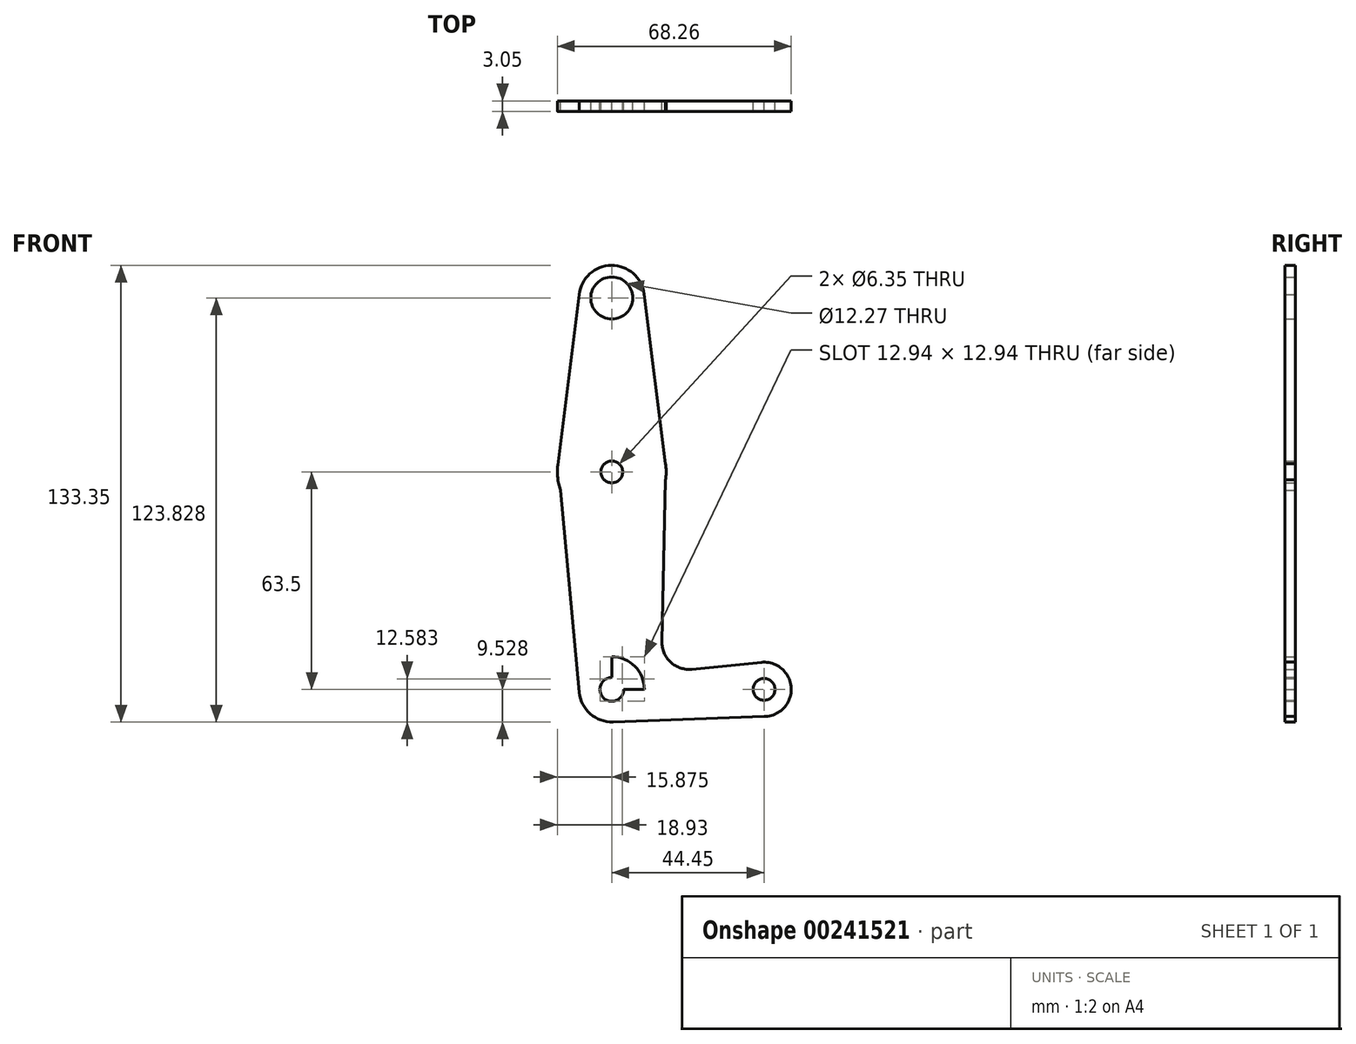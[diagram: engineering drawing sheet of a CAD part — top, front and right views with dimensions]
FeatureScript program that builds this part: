
annotation { "Feature Type Name" : "Feature", "Feature Type Description" : "" }
export const myFeature = defineFeature(function(context is Context, id is Id, definition is map)
    precondition{}
    {
        {
            var Q0;
            Q0=qCreatedBy(makeId("Front.planeOp"),FACE);
            var sketch = newSketch(context, id + "F0", { "sketchPlane" : qUnion([Q0])});
            skLineSegment(sketch, "E0", {"start": v(-63.28, 63.3) * mm, "end": v(-63.28, -51) * mm});
            skLineSegment(sketch, "E1", {"start": v(-63.28, -51) * mm, "end": v(-18.83, -51) * mm});
            skCircle(sketch, "E2", {"center": v(-63.28, 63.3) * mm, "radius": 9.53 * mm});
            skCircle(sketch, "E3", {"center": v(-63.28, 12.5) * mm, "radius": 15.88 * mm});
            skCircle(sketch, "E4", {"center": v(-63.28, -51) * mm, "radius": 9.53 * mm});
            skCircle(sketch, "E5", {"center": v(-18.83, -51) * mm, "radius": 7.94 * mm});
            skLineSegment(sketch, "E6", {"start": v(-41.05, -51) * mm, "end": v(-56.61, -51) * mm});
            skLineSegment(sketch, "E7", {"start": v(-63.28, 12.5) * mm, "end": v(-63.28, -51) * mm});
            skLineSegment(sketch, "E8", {"start": v(-72.75, 64.3) * mm, "end": v(-79.03, 14.48) * mm});
            skLineSegment(sketch, "E9", {"start": v(-78.24, 7.21) * mm, "end": v(-72.76, -51.88) * mm});
            skLineSegment(sketch, "E10", {"start": v(-47.48, 14.1) * mm, "end": v(-53.82, 64.49) * mm});
            skCircle(sketch, "E11", {"center": v(-63.28, 63.3) * mm, "radius": 6.13 * mm});
            skCircle(sketch, "E12", {"center": v(-63.28, 12.5) * mm, "radius": 3.18 * mm});
            skCircle(sketch, "E13", {"center": v(-63.28, -51) * mm, "radius": 3.48 * mm});
            skCircle(sketch, "E14", {"center": v(-18.83, -51) * mm, "radius": 3.18 * mm});
            skLineSegment(sketch, "E15", {"start": v(-18.83, -58.94) * mm, "end": v(-62.93, -60.52) * mm});
            skLineSegment(sketch, "E16", {"start": v(-19.62, -43.1) * mm, "end": v(-39.89, -45.14) * mm});
            skPoint(sketch, "E16.endSnap0", {"position": v(-48.83, -51) * mm});
            skLineSegment(sketch, "E17", {"start": v(-47.48, 14.1) * mm, "end": v(-48.63, -37.05) * mm});
            skPoint(sketch, "E18.visualSharp", {"position": v(-48.83, -46.03) * mm});
            skLineSegment(sketch, "E18.filletArc", {"start": v(-48.83, -46.03) * mm, "end": v(-48.83, -46.03) * mm});
            skArc(sketch, "E19.filletArc", {"start": v(-48.63, -37.05) * mm, "mid": v(-46.08, -43.06) * mm, "end": v(-39.89, -45.14) * mm});
            skSolve(sketch);
        }
        {
            var Q0;
            Q0 = qSketchRegion(id + "F0", true);
            extrude(context, id + "F1", {"entities" : qUnion([Q0]), "depth" : 3.05 * mm});
        }
    });
